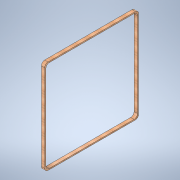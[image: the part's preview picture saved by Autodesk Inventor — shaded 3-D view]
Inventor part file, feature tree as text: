
AUTODESK INVENTOR PART (.ipt)
format: ipt  version: 2022 (Build 260153000, 153)  size: 123,392 bytes
history: native  units: in
note: dims shown in document units (in); Inventor stores cm internally (conversion verified against a paired STEP export)
features: helix x1, extrude x1, sketch x1
ambient origin geometry x8: Origin, YZ Plane, XZ Plane, XY Plane, X Axis, Y Axis, Z Axis, Center Point
bodies: Solid1 (feature_tree)
feature tree (3):
  helix  "Coil3or4"  [1 undecoded]
  extrude  "Extrusion1"  Depth=75.1969in
  sketch  "Sketch1"  dims[d1=77.1654in d2=75.1969in d3=75.1969in d4=2.7559in d5=2.7559in d6=0.0in]
note: 1 required parameter value undecoded (feature->parameter linkage not recoverable at this tier; creation-order binding heuristic only, values carry confidence <= 0.55)
